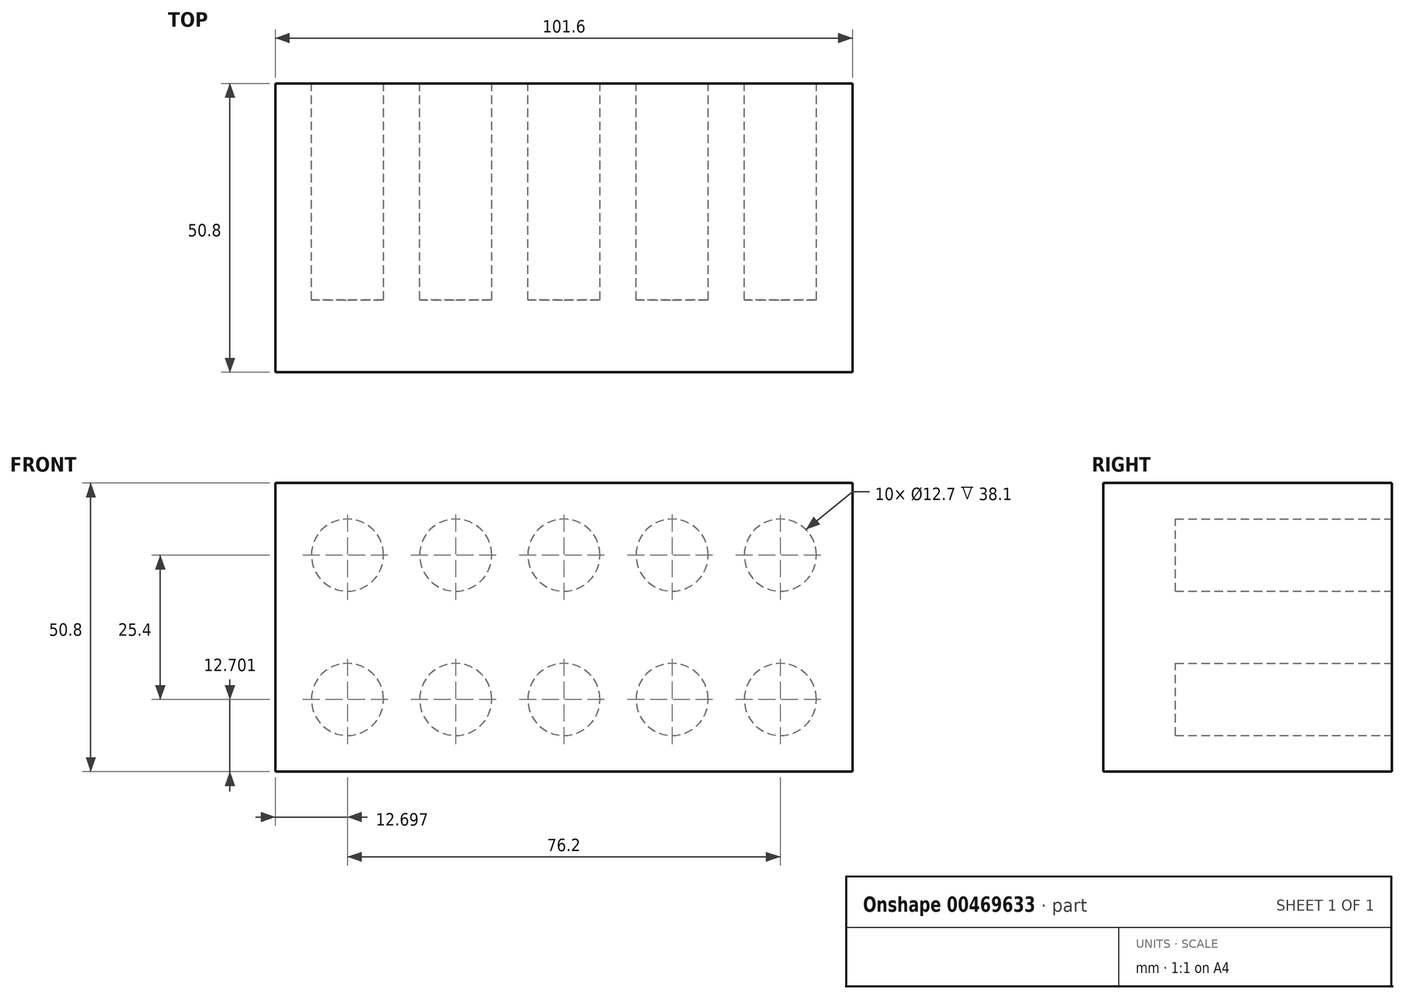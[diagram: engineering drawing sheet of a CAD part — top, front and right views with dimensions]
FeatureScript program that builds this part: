
annotation { "Feature Type Name" : "Feature", "Feature Type Description" : "" }
export const myFeature = defineFeature(function(context is Context, id is Id, definition is map)
    precondition{}
    {
        {
            var Q0;
            Q0=qCreatedBy(makeId("Front.planeOp"),FACE);
            var sketch = newSketch(context, id + "F0", { "sketchPlane" : qUnion([Q0])});
            skLineSegment(sketch, "E0.bottom", {"start": v(-31.92, 16.02) * mm, "end": v(69.68, 16.02) * mm});
            skLineSegment(sketch, "E0.top", {"start": v(-31.92, -34.78) * mm, "end": v(69.68, -34.78) * mm});
            skLineSegment(sketch, "E0.left", {"start": v(-31.92, 16.02) * mm, "end": v(-31.92, -34.78) * mm});
            skLineSegment(sketch, "E0.right", {"start": v(69.68, 16.02) * mm, "end": v(69.68, -34.78) * mm});
            skSolve(sketch);
        }
        {
            var Q0;
            Q0 = qSketchRegion(id + "F0", true);
            extrude(context, id + "F1", {"entities" : qUnion([Q0]), "depth" : 50.8 * mm});
        }
        {
            var Q0;
            Q0=qCreatedBy(makeId("Front.planeOp"),FACE);
            var sketch = newSketch(context, id + "F2", { "sketchPlane" : qUnion([Q0])});
            skCircle(sketch, "E1", {"center": v(-19.22, 3.32) * mm, "radius": 6.35 * mm});
            skCircle(sketch, "E2", {"center": v(-19.22, -22.08) * mm, "radius": 6.35 * mm});
            skPoint(sketch, "E3.center.orphan", {"position": v(0, -3.03) * mm});
            skCircle(sketch, "E4", {"center": v(-0.17, 3.32) * mm, "radius": 6.35 * mm});
            skCircle(sketch, "E5", {"center": v(-0.17, -22.08) * mm, "radius": 6.35 * mm});
            skCircle(sketch, "E6", {"center": v(18.88, 3.32) * mm, "radius": 6.35 * mm});
            skCircle(sketch, "E7", {"center": v(18.88, -22.08) * mm, "radius": 6.35 * mm});
            skCircle(sketch, "E8", {"center": v(37.93, -22.08) * mm, "radius": 6.35 * mm});
            skCircle(sketch, "E9", {"center": v(37.93, 3.32) * mm, "radius": 6.35 * mm});
            skCircle(sketch, "E10", {"center": v(56.98, 3.32) * mm, "radius": 6.35 * mm});
            skCircle(sketch, "E11", {"center": v(56.98, -22.08) * mm, "radius": 6.35 * mm});
            skSolve(sketch);
        }
        {
            var Q0;
            Q0 = qSketchRegion(id + "F2", true);
            extrude(context, id + "F3", {"entities" : qUnion([Q0]), "operationType" : NewBodyOperationType.REMOVE, "depth" : 38.1 * mm});
        }
    });
